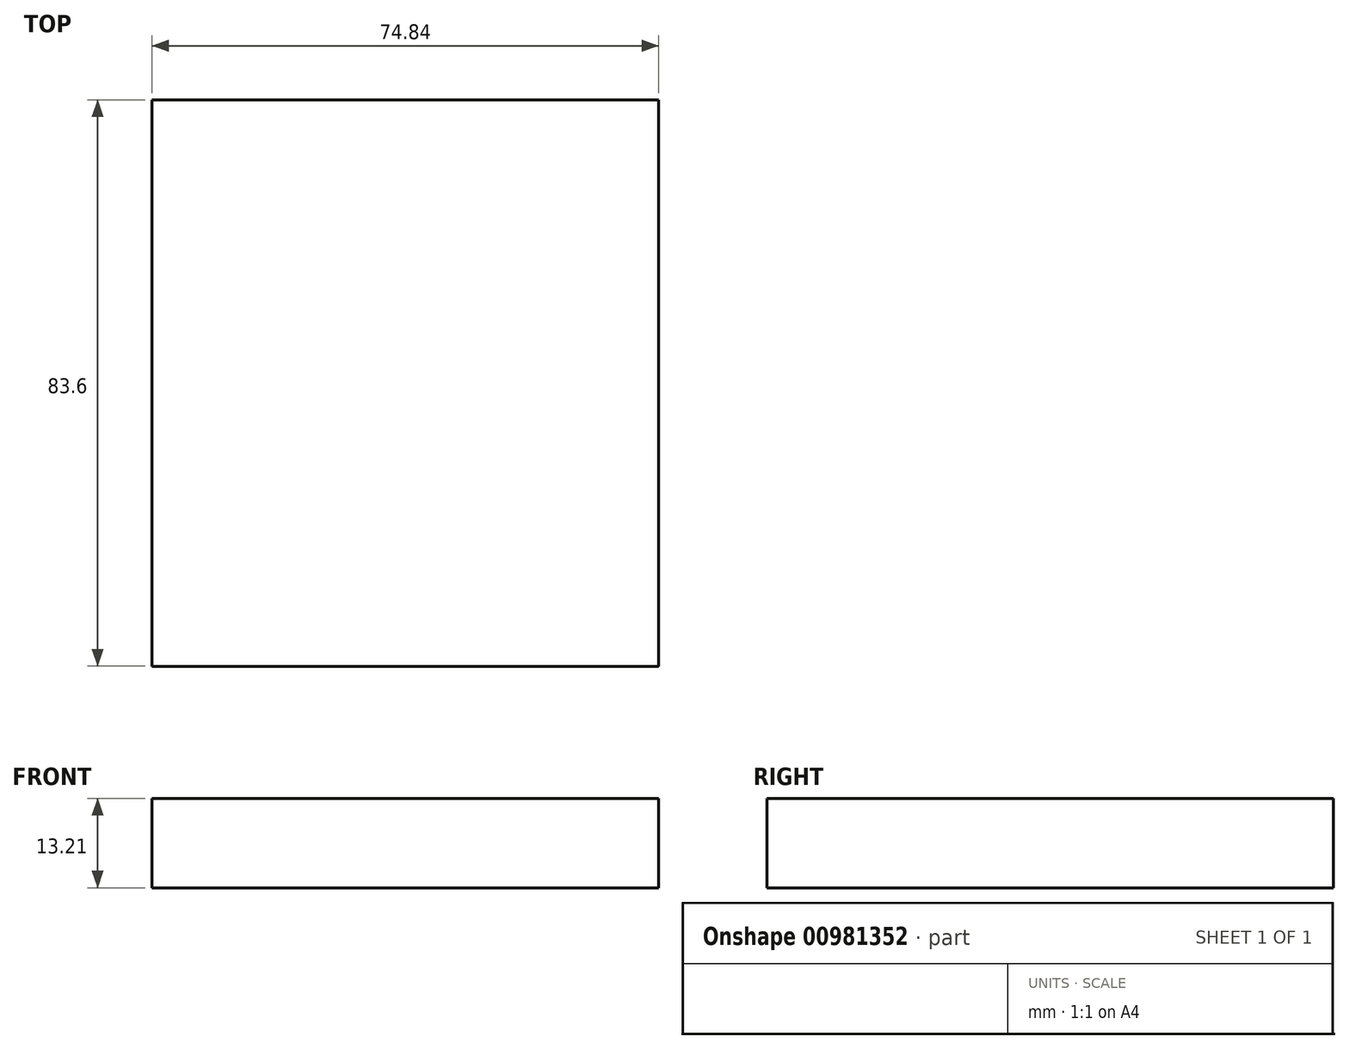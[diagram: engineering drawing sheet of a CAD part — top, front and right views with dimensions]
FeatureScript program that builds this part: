
annotation { "Feature Type Name" : "Feature", "Feature Type Description" : "" }
export const myFeature = defineFeature(function(context is Context, id is Id, definition is map)
    precondition{}
    {
        {
            var Q0;
            Q0=qCreatedBy(makeId("Top.planeOp"),FACE);
            var sketch = newSketch(context, id + "F0", { "sketchPlane" : qUnion([Q0])});
            skLineSegment(sketch, "E0.bottom", {"start": v(-116.18, -52.6) * mm, "end": v(-41.34, -52.6) * mm});
            skLineSegment(sketch, "E0.top", {"start": v(-116.18, 31.01) * mm, "end": v(-41.34, 31.01) * mm});
            skLineSegment(sketch, "E0.left", {"start": v(-116.18, -52.6) * mm, "end": v(-116.18, 31.01) * mm});
            skLineSegment(sketch, "E0.right", {"start": v(-41.34, -52.6) * mm, "end": v(-41.34, 31.01) * mm});
            skSolve(sketch);
        }
        {
            var Q0;
            Q0=makeQuery(id+"F0.imprint","IMPRINT",FACE,{"disambiguationData":[TD([[makeQuery(id+"F0.imprint","IMPRINT",EDGE,{"derivedFrom":sQuery(id+"F0.wireOp",EDGE,"E0.bottom")}),1.0]])]});
            extrude(context, id + "F1", {"entities" : qUnion([Q0]), "depth" : 9.4 * mm, "offsetDistance" : 25.4 * mm});
        }
        {
            var Q0;
            Q0=makeQuery(id+"F1.opExtrude","CAP_FACE",FACE,{"disambiguationData":[OSD([sQuery(id+"F0.wireOp",EDGE,"E0.bottom"),sQuery(id+"F0.wireOp",EDGE,"E0.top"),sQuery(id+"F0.wireOp",EDGE,"E0.left"),sQuery(id+"F0.wireOp",EDGE,"E0.right")])],"isStart":false});
            extrude(context, id + "F2", {"entities" : qUnion([Q0]), "operationType" : NewBodyOperationType.ADD, "oppositeDirection" : true, "depth" : 13.2 * mm, "offsetDistance" : 25.4 * mm});
        }
    });
